# Revit family: Bath-Drop_In-Kohler-Mariposa-K_1242
name_source: partatom
category: Plumbing Fixtures
revit_build: Autodesk Revit 2015 (Build: 20140606_1530(x64)
units: mm (PartAtom-declared; Revit-internal decimal feet)

## types (5) — shared parameters
Assembly Code = D2010510
CW Connection = No
Default Elevation = 0' - 0"
Drain Diameter = 0' - 1 1/2"
HW Connection = No
Height = 1' - 8"
Keynote = 22 40 00.D2
Length = 5' - 0"
Manufacturer = Kohler
Material = Acrylic
Product Documentation Link = http://www.us.kohler.com
Product Name = Mariposa 60'' x 36'' Drop-In Bath
Product Page URL = http://www.us.kohler.com
Sanitary Connector = Sanitary Drain
URL = http://www.us.kohler.com
Vent Connection = Yes
Version = 2014 - v1.0a
Waste Connection = Yes
Water Capacity = 63 gal (238.5 L)
Weight = 62 lbs (28.1 kg)
Width = 3' - 0"
zero-valued in all types: CWFU, HWFU, WFU

## per-type parameters (varying)
| type | ADA Compliant | ControlM | Description | Finish | Model |
| 0-White | No | 0 | 60'' x 36'' Drop-in Bath with Reversible Drain, White | Acrylic - Kohler - 0 - White | K-1242-0 |
| 47-Almond | Yes | 47 | 60'' x 36'' Drop-in Bath with Reversible Drain, Almond | Acrylic - Kohler - 47 - Almond | K-1242-47 |
| 96-Biscuit | Yes | 96 | 60'' x 36'' Drop-in Bath with Reversible Drain, Biscuit | Acrylic - Kohler - 96 - Biscuit | K-1242-96 |
| G9-Sandbar | Yes | 79 | 60'' x 36'' Drop-in Bath with Reversible Drain, Sandbar | Acrylic - Kohler - G9 - Sandbar | K-1242-G9 |
| NY-Dune | Yes | 1425 | 60'' x 36'' Drop-in Bath with Reversible Drain, Dune | Acrylic - Kohler - NY - Dune | K-1242-NY |

## geometry (parser evidence)
native form markers: Extrusion x5, Sweep x2
no freeform markers — native parametric forms only
